# Revit family: RN 85169 Optiflex-Profix-Raccord-Té coude
name_source: partatom
category: Rohrformteile
units: mm (PartAtom-declared; Revit-internal decimal feet)

## family parameters
Arbeitsebenenbasiert = Nein
Beim Laden mit Abzugskörper schneiden = Nein
Bemaßung runder Anschluss = Durchmesser verwenden
Gemeinsam genutzt = Nein
Immer vertikal = Ja
Teiletyp = T-Stück

## types (1)
- DN=20x15x15
    1.010.00.2 Blattnummer der Richtlinie = 29
    1.010.00.3 Ausgabedatum (Monat) der Richtlinie = 201308
    1.010.00.4 Herstellername = R. Nussbaum AG
    1.010.00.5 Revisionsdatum der Datei = 20190521
    1.010.00.6 Webadresse des Herstellers = http://www.nussbaum.ch
    1.100.00.4 Produktbezeichnung = Versorgung
    1.110.00.2 Index = 5
    1.110.00.4 Produktbezeichnung = Optiflex
    1.800.00.3 TGA-Nummer = 01900500000000000000000000000000000000000000000094000000000000000001
    1.800.00.4 Kommentarfeld = 85169.21, Optiflex-P-Erweiterungs-Verteilstück, mit loser Mutter, DN=20x15x15, L=50
    1.810.00.3 Hersteller-Bestellnummer = 85169.21
    1.810.00.4 DATANORM-Nummer = 85169.21
    1.810.00.6 GTIN-Nummer = 7612945818522
    1.960/3L.00.8 Link (URL) = https://www.nussbaum.ch
    29.700.00.4 Produktname = Optiflex-P-Erweiterungs-Verteilstück, mit loser Mutter
    29.700.00.5 Produktkennung = 2
    29.700.00.6 Querschnittsform = 1
    29.700.00.7 Nennweitensystem = DN
    29.700.00.8 Nenndrucksystem = PN
    29.710.02.10 Formstück-Gewicht [kg] = 0.279
    29.710.02.3 Benennung = Optiflex-P-Erweiterungs-Verteilstück, mit loser Mutter, DN=20x15x15, L=50
    29.710.02.4 Nenndruck = 10
    29.710.02.5 max. zul. Überdruck [hPa] = 1000
    29.710.02.7 max. zul. Dauer-Betriebsdruck [hPa] = 1000
    29.710.02.9 max. zul. Dauer-Betriebstemperatur [°C] = 70
    CONNECTOR0_DIAMETER_dX_0r = 20 mm
    CONNECTOR0_dX_00 = 78 mm
    CONNECTOR0_dX_01 = 93 mm
    CONNECTOR0_ref_dX = 78 mm
    CONNECTOR1_DIAMETER_dX_0r = 12 mm  [stored 0.0393701 ft]
    CONNECTOR1_dX_01 = 34 mm
    CONNECTOR1_ref_dX = 34 mm
    CONNECTOR1_ref_dY = 50 mm  [stored 0.164042 ft]
    CONNECTOR2_DIAMETER_dX_0r = 12 mm  [stored 0.0393701 ft]
    CONNECTOR2_dX_01 = 34 mm
    CONNECTOR2_ref_dX = 34 mm
    Connector Visibility = Nein
    EnclosingSpace Visibility = Nein
    Hersteller = R. Nussbaum AG
    Modell = 85169.21
    R. Nussbaum AG 85169.21 de Visibility = Ja
    Typenkommentare = Optiflex-Profix-Raccord-Té coude  DN=20x15x15
    URL = https://www.nussbaum.ch

note: [stored X ft] marks values corroborated as IEEE doubles in the binary element streams (Revit-internal decimal feet)

## geometry (parser evidence)
native form markers: Sweep x3
no freeform markers — native parametric forms only
